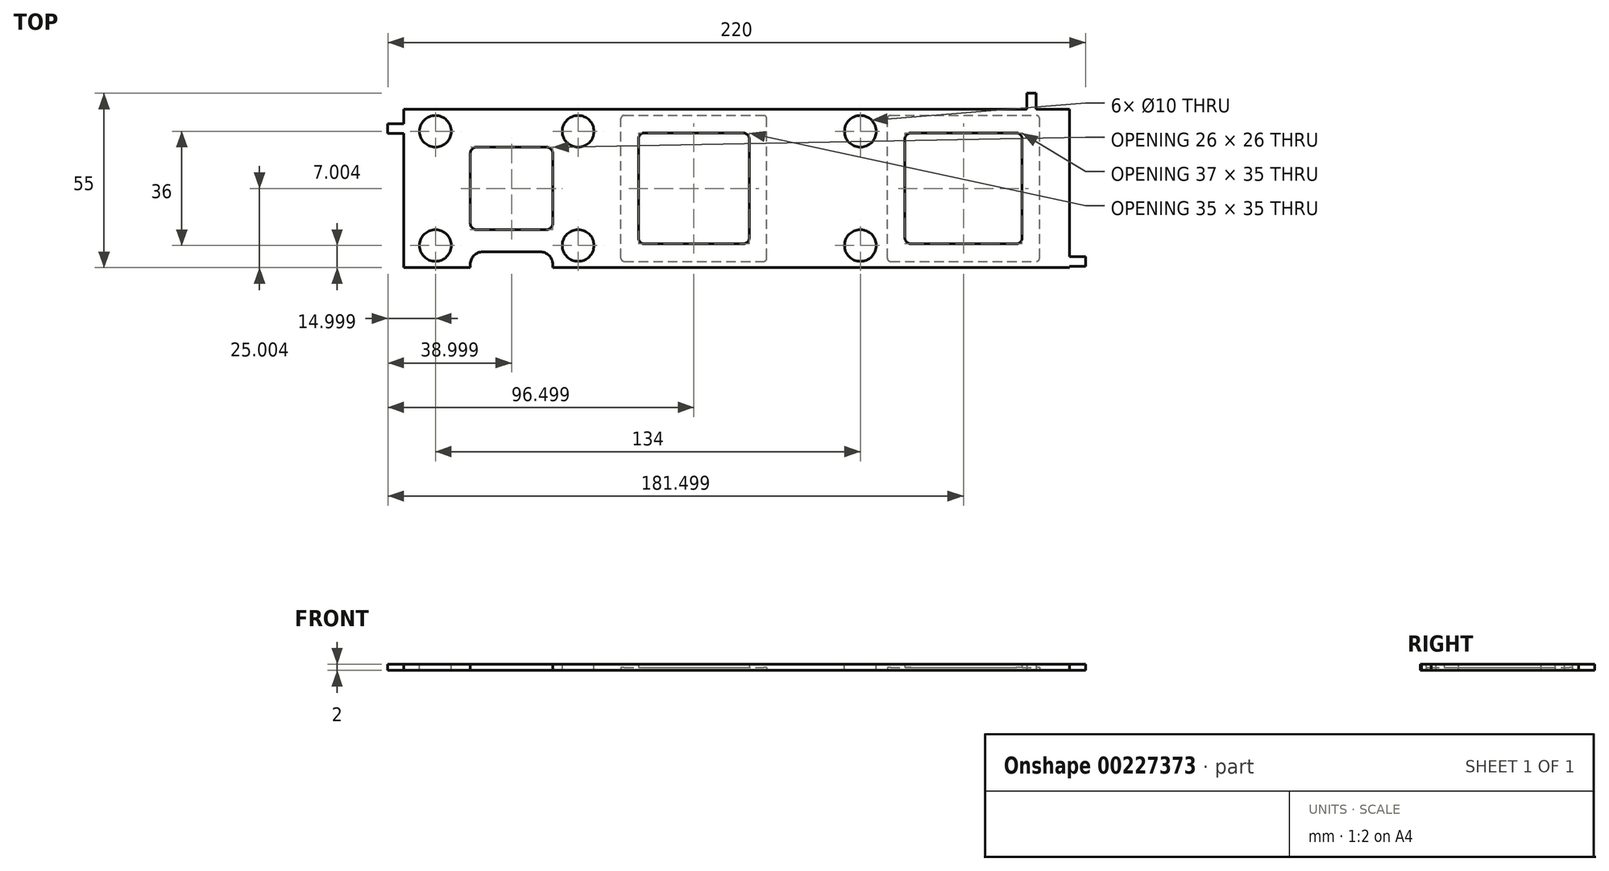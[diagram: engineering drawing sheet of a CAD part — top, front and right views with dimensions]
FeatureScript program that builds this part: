
annotation { "Feature Type Name" : "Feature", "Feature Type Description" : "" }
export const myFeature = defineFeature(function(context is Context, id is Id, definition is map)
    precondition{}
    {
        {
            var Q0;
            Q0=qCreatedBy(makeId("Top.planeOp"),FACE);
            var sketch = newSketch(context, id + "F0", { "sketchPlane" : qUnion([Q0])});
            skLineSegment(sketch, "E0.bottom", {"start": v(-23.9, 18.14) * mm, "end": v(186.1, 18.14) * mm});
            skLineSegment(sketch, "E0.top", {"start": v(-23.9, -31.86) * mm, "end": v(186.1, -31.86) * mm});
            skLineSegment(sketch, "E0.left", {"start": v(-23.9, 18.14) * mm, "end": v(-23.9, -31.86) * mm});
            skLineSegment(sketch, "E0.right", {"start": v(186.1, 18.14) * mm, "end": v(186.1, -31.86) * mm});
            skPoint(sketch, "E1.oppositeSnap0", {"position": v(-26.4, 18.14) * mm});
            skLineSegment(sketch, "E1.bottom", {"start": v(172.54, 23.14) * mm, "end": v(175.54, 23.14) * mm});
            skLineSegment(sketch, "E1.top", {"start": v(172.54, 18.14) * mm, "end": v(175.54, 18.14) * mm});
            skLineSegment(sketch, "E1.left", {"start": v(172.54, 23.14) * mm, "end": v(172.54, 18.14) * mm});
            skLineSegment(sketch, "E1.right", {"start": v(175.54, 23.14) * mm, "end": v(175.54, 18.14) * mm});
            skLineSegment(sketch, "E2.bottom", {"start": v(-9.51, -31.86) * mm, "end": v(-6.51, -31.86) * mm});
            skLineSegment(sketch, "E2.top", {"start": v(-9.51, -36.86) * mm, "end": v(-6.51, -36.86) * mm});
            skLineSegment(sketch, "E2.left", {"start": v(-9.51, -31.86) * mm, "end": v(-9.51, -36.86) * mm});
            skLineSegment(sketch, "E2.right", {"start": v(-6.51, -31.86) * mm, "end": v(-6.51, -36.86) * mm});
            skLineSegment(sketch, "E3.bottom", {"start": v(186.1, -28.4) * mm, "end": v(191.1, -28.4) * mm});
            skLineSegment(sketch, "E3.top", {"start": v(186.1, -31.4) * mm, "end": v(191.1, -31.4) * mm});
            skLineSegment(sketch, "E3.left", {"start": v(186.1, -28.4) * mm, "end": v(186.1, -31.4) * mm});
            skLineSegment(sketch, "E3.right", {"start": v(191.1, -28.4) * mm, "end": v(191.1, -31.4) * mm});
            skLineSegment(sketch, "E4.bottom", {"start": v(-28.9, 10.54) * mm, "end": v(-23.9, 10.54) * mm});
            skLineSegment(sketch, "E4.top", {"start": v(-28.9, 13.54) * mm, "end": v(-23.9, 13.54) * mm});
            skLineSegment(sketch, "E4.left", {"start": v(-28.9, 10.54) * mm, "end": v(-28.9, 13.54) * mm});
            skLineSegment(sketch, "E4.right", {"start": v(-23.9, 10.54) * mm, "end": v(-23.9, 13.54) * mm});
            skSolve(sketch);
        }
        {
            var Q0;
            Q0=makeQuery(id+"F0.imprint","IMPRINT",FACE,{"disambiguationData":[TD([[makeQuery(id+"F0.imprint","IMPRINT",EDGE,{"derivedFrom":sQuery(id+"F0.wireOp",EDGE,"E0.bottom")}),-1.0]])]});
            extrude(context, id + "F1", {"entities" : qUnion([Q0]), "depth" : 2 * mm});
        }
        {
            var Q0;
            Q0=makeQuery(id+"F1.opExtrude","CAP_FACE",FACE,{"disambiguationData":[OSD([sQuery(id+"F0.wireOp",EDGE,"E0.bottom"),sQuery(id+"F0.wireOp",EDGE,"E0.top"),sQuery(id+"F0.wireOp",EDGE,"E0.left"),sQuery(id+"F0.wireOp",EDGE,"E0.right")])],"isStart":true});
            var sketch = newSketch(context, id + "F2", { "sketchPlane" : qUnion([Q0])});
            skLineSegment(sketch, "E5.bottom", {"start": v(-2.9, 19.86) * mm, "end": v(23.1, 19.86) * mm});
            skLineSegment(sketch, "E5.top", {"start": v(-2.9, -6.14) * mm, "end": v(23.1, -6.14) * mm});
            skLineSegment(sketch, "E5.left", {"start": v(-2.9, 19.86) * mm, "end": v(-2.9, -6.14) * mm});
            skLineSegment(sketch, "E5.right", {"start": v(23.1, 19.86) * mm, "end": v(23.1, -6.14) * mm});
            skSolve(sketch);
        }
        {
            var Q0;
            Q0=makeQuery(id+"F2.imprint","IMPRINT",FACE,{"disambiguationData":[TD([[makeQuery(id+"F2.imprint","IMPRINT",EDGE,{"derivedFrom":sQuery(id+"F2.wireOp",EDGE,"E5.bottom")}),-1.0]])]});
            extrude(context, id + "F3", {"entities" : qUnion([Q0]), "operationType" : NewBodyOperationType.REMOVE, "oppositeDirection" : true, "depth" : 15.4 * mm});
        }
        {
            var Q0;
            Q0=makeQuery(id+"F1.opExtrude","CAP_FACE",FACE,{"disambiguationData":[OSD([sQuery(id+"F0.wireOp",EDGE,"E0.bottom"),sQuery(id+"F0.wireOp",EDGE,"E0.top"),sQuery(id+"F0.wireOp",EDGE,"E0.left"),sQuery(id+"F0.wireOp",EDGE,"E0.right")])],"isStart":true});
            var sketch = newSketch(context, id + "F4", { "sketchPlane" : qUnion([Q0])});
            skLineSegment(sketch, "E6.bottom", {"start": v(50.1, 24.36) * mm, "end": v(85.1, 24.36) * mm});
            skLineSegment(sketch, "E6.top", {"start": v(50.1, -10.64) * mm, "end": v(85.1, -10.64) * mm});
            skLineSegment(sketch, "E6.left", {"start": v(50.1, 24.36) * mm, "end": v(50.1, -10.64) * mm});
            skLineSegment(sketch, "E6.right", {"start": v(85.1, 24.36) * mm, "end": v(85.1, -10.64) * mm});
            skLineSegment(sketch, "E7.bottom", {"start": v(134.1, 24.36) * mm, "end": v(171.1, 24.36) * mm});
            skLineSegment(sketch, "E7.top", {"start": v(134.1, -10.64) * mm, "end": v(171.1, -10.64) * mm});
            skLineSegment(sketch, "E7.left", {"start": v(134.1, 24.36) * mm, "end": v(134.1, -10.64) * mm});
            skLineSegment(sketch, "E7.right", {"start": v(171.1, 24.36) * mm, "end": v(171.1, -10.64) * mm});
            skSolve(sketch);
        }
        {
            var Q0;
            Q0=makeQuery(id+"F4.imprint","IMPRINT",FACE,{"disambiguationData":[TD([[makeQuery(id+"F4.imprint","IMPRINT",EDGE,{"derivedFrom":sQuery(id+"F4.wireOp",EDGE,"E6.bottom")}),-1.0]])]});
            var Q1;
            Q1=makeQuery(id+"F4.imprint","IMPRINT",FACE,{"disambiguationData":[TD([[makeQuery(id+"F4.imprint","IMPRINT",EDGE,{"derivedFrom":sQuery(id+"F4.wireOp",EDGE,"E7.bottom")}),-1.0]])]});
            extrude(context, id + "F5", {"entities" : qUnion([Q0, Q1]), "operationType" : NewBodyOperationType.REMOVE, "oppositeDirection" : true, "depth" : 25 * mm});
        }
        {
            var Q0;
            Q0=makeQuery(id+"F1.opExtrude","CAP_FACE",FACE,{"disambiguationData":[OSD([sQuery(id+"F0.wireOp",EDGE,"E0.bottom"),sQuery(id+"F0.wireOp",EDGE,"E0.top"),sQuery(id+"F0.wireOp",EDGE,"E0.left"),sQuery(id+"F0.wireOp",EDGE,"E0.right")])],"isStart":false});
            var sketch = newSketch(context, id + "F6", { "sketchPlane" : qUnion([Q0])});
            skLineSegment(sketch, "E8.bottom", {"start": v(-2.9, -26.86) * mm, "end": v(23.1, -26.86) * mm});
            skLineSegment(sketch, "E8.top", {"start": v(-2.9, -31.86) * mm, "end": v(23.1, -31.86) * mm});
            skLineSegment(sketch, "E8.left", {"start": v(-2.9, -26.86) * mm, "end": v(-2.9, -31.86) * mm});
            skLineSegment(sketch, "E8.right", {"start": v(23.1, -26.86) * mm, "end": v(23.1, -31.86) * mm});
            skSolve(sketch);
        }
        {
            var Q0;
            Q0=makeQuery(id+"F6.imprint","IMPRINT",FACE,{"disambiguationData":[TD([[makeQuery(id+"F6.imprint","IMPRINT",EDGE,{"derivedFrom":sQuery(id+"F6.wireOp",EDGE,"E8.bottom")}),-1.0]])]});
            extrude(context, id + "F7", {"entities" : qUnion([Q0]), "operationType" : NewBodyOperationType.REMOVE, "oppositeDirection" : true, "depth" : 25 * mm});
        }
        {
            var Q0;
            Q0=makeQuery(id+"F7.boolean.opBoolean","COPY",EDGE,{"derivedFrom":makeQuery(id+"F7.opExtrude","SWEPT_EDGE",EDGE,{"disambiguationData":[OSD([sQuery(id+"F6.wireOp",EDGE,"E8.bottom"),sQuery(id+"F6.wireOp",EDGE,"E8.left")])]})});
            var Q1;
            Q1=makeQuery(id+"F7.boolean.opBoolean","COPY",EDGE,{"derivedFrom":makeQuery(id+"F7.opExtrude","SWEPT_EDGE",EDGE,{"disambiguationData":[OSD([sQuery(id+"F6.wireOp",EDGE,"E8.bottom"),sQuery(id+"F6.wireOp",EDGE,"E8.right")])]})});
            fillet(context, id + "F8", {"entities" : qUnion([Q0, Q1]), "radius" : 4 * mm, "tangentPropagation" : true, "allowEdgeOverflow" : false});
        }
        {
            var Q0;
            Q0=makeQuery(id+"F5.boolean.opBoolean","COPY",EDGE,{"derivedFrom":makeQuery(id+"F5.opExtrude","SWEPT_EDGE",EDGE,{"disambiguationData":[OSD([sQuery(id+"F4.wireOp",EDGE,"E6.top"),sQuery(id+"F4.wireOp",EDGE,"E6.left")])]})});
            var Q1;
            Q1=makeQuery(id+"F5.boolean.opBoolean","COPY",EDGE,{"derivedFrom":makeQuery(id+"F5.opExtrude","SWEPT_EDGE",EDGE,{"disambiguationData":[OSD([sQuery(id+"F4.wireOp",EDGE,"E6.top"),sQuery(id+"F4.wireOp",EDGE,"E6.right")])]})});
            var Q2;
            Q2=makeQuery(id+"F5.boolean.opBoolean","COPY",EDGE,{"derivedFrom":makeQuery(id+"F5.opExtrude","SWEPT_EDGE",EDGE,{"disambiguationData":[OSD([sQuery(id+"F4.wireOp",EDGE,"E6.bottom"),sQuery(id+"F4.wireOp",EDGE,"E6.left")])]})});
            var Q3;
            Q3=makeQuery(id+"F5.boolean.opBoolean","COPY",EDGE,{"derivedFrom":makeQuery(id+"F5.opExtrude","SWEPT_EDGE",EDGE,{"disambiguationData":[OSD([sQuery(id+"F4.wireOp",EDGE,"E7.bottom"),sQuery(id+"F4.wireOp",EDGE,"E7.left")])]})});
            var Q4;
            Q4=makeQuery(id+"F5.boolean.opBoolean","COPY",EDGE,{"derivedFrom":makeQuery(id+"F5.opExtrude","SWEPT_EDGE",EDGE,{"disambiguationData":[OSD([sQuery(id+"F4.wireOp",EDGE,"E6.bottom"),sQuery(id+"F4.wireOp",EDGE,"E6.right")])]})});
            var Q5;
            Q5=makeQuery(id+"F5.boolean.opBoolean","COPY",EDGE,{"derivedFrom":makeQuery(id+"F5.opExtrude","SWEPT_EDGE",EDGE,{"disambiguationData":[OSD([sQuery(id+"F4.wireOp",EDGE,"E7.bottom"),sQuery(id+"F4.wireOp",EDGE,"E7.right")])]})});
            var Q6;
            Q6=makeQuery(id+"F5.boolean.opBoolean","COPY",EDGE,{"derivedFrom":makeQuery(id+"F5.opExtrude","SWEPT_EDGE",EDGE,{"disambiguationData":[OSD([sQuery(id+"F4.wireOp",EDGE,"E7.top"),sQuery(id+"F4.wireOp",EDGE,"E7.left")])]})});
            var Q7;
            Q7=makeQuery(id+"F5.boolean.opBoolean","COPY",EDGE,{"derivedFrom":makeQuery(id+"F5.opExtrude","SWEPT_EDGE",EDGE,{"disambiguationData":[OSD([sQuery(id+"F4.wireOp",EDGE,"E7.top"),sQuery(id+"F4.wireOp",EDGE,"E7.right")])]})});
            var Q8;
            Q8=makeQuery(id+"F3.boolean.opBoolean","COPY",EDGE,{"derivedFrom":makeQuery(id+"F3.opExtrude","SWEPT_EDGE",EDGE,{"disambiguationData":[OSD([sQuery(id+"F2.wireOp",EDGE,"E5.top"),sQuery(id+"F2.wireOp",EDGE,"E5.right")])]})});
            var Q9;
            Q9=makeQuery(id+"F3.boolean.opBoolean","COPY",EDGE,{"derivedFrom":makeQuery(id+"F3.opExtrude","SWEPT_EDGE",EDGE,{"disambiguationData":[OSD([sQuery(id+"F2.wireOp",EDGE,"E5.top"),sQuery(id+"F2.wireOp",EDGE,"E5.left")])]})});
            var Q10;
            Q10=makeQuery(id+"F3.boolean.opBoolean","COPY",EDGE,{"derivedFrom":makeQuery(id+"F3.opExtrude","SWEPT_EDGE",EDGE,{"disambiguationData":[OSD([sQuery(id+"F2.wireOp",EDGE,"E5.bottom"),sQuery(id+"F2.wireOp",EDGE,"E5.right")])]})});
            var Q11;
            Q11=makeQuery(id+"F3.boolean.opBoolean","COPY",EDGE,{"derivedFrom":makeQuery(id+"F3.opExtrude","SWEPT_EDGE",EDGE,{"disambiguationData":[OSD([sQuery(id+"F2.wireOp",EDGE,"E5.bottom"),sQuery(id+"F2.wireOp",EDGE,"E5.left")])]})});
            fillet(context, id + "F9", {"entities" : qUnion([Q0, Q1, Q2, Q3, Q4, Q5, Q6, Q7, Q8, Q9, Q10, Q11]), "radius" : 2 * mm, "tangentPropagation" : true, "allowEdgeOverflow" : false});
        }
        {
            var Q0;
            Q0=makeQuery(id+"F1.opExtrude","CAP_FACE",FACE,{"disambiguationData":[OSD([sQuery(id+"F0.wireOp",EDGE,"E0.bottom"),sQuery(id+"F0.wireOp",EDGE,"E0.top"),sQuery(id+"F0.wireOp",EDGE,"E0.left"),sQuery(id+"F0.wireOp",EDGE,"E0.right")])],"isStart":false});
            var sketch = newSketch(context, id + "F10", { "sketchPlane" : qUnion([Q0])});
            skCircle(sketch, "E9", {"center": v(-13.9, 11.14) * mm, "radius": 5 * mm});
            skCircle(sketch, "E10", {"center": v(-13.9, -24.86) * mm, "radius": 5 * mm});
            skCircle(sketch, "E11", {"center": v(31.1, -24.86) * mm, "radius": 5 * mm});
            skCircle(sketch, "E12", {"center": v(120.1, 11.14) * mm, "radius": 5 * mm});
            skCircle(sketch, "E13", {"center": v(120.1, -24.86) * mm, "radius": 5 * mm});
            skSolve(sketch);
        }
        {
            var Q0;
            Q0=makeQuery(id+"F10.imprint","IMPRINT",FACE,{"disambiguationData":[TD([[makeQuery(id+"F10.imprint","IMPRINT",EDGE,{"derivedFrom":sQuery(id+"F10.wireOp",EDGE,"E12")}),1.0]])]});
            var Q1;
            Q1=makeQuery(id+"F10.imprint","IMPRINT",FACE,{"disambiguationData":[TD([[makeQuery(id+"F10.imprint","IMPRINT",EDGE,{"derivedFrom":sQuery(id+"F10.wireOp",EDGE,"E13")}),1.0]])]});
            var Q2;
            Q2=makeQuery(id+"F10.imprint","IMPRINT",FACE,{"disambiguationData":[TD([[makeQuery(id+"F10.imprint","IMPRINT",EDGE,{"derivedFrom":sQuery(id+"F10.wireOp",EDGE,"E11")}),1.0]])]});
            var Q3;
            Q3=makeQuery(id+"F10.imprint","IMPRINT",FACE,{"disambiguationData":[TD([[makeQuery(id+"F10.imprint","IMPRINT",EDGE,{"derivedFrom":sQuery(id+"F10.wireOp",EDGE,"izE0OuF1-xiSJ-FB18-c39p-0N1t3OY4qnCi")}),1.0]])]});
            var Q4;
            Q4=makeQuery(id+"F10.imprint","IMPRINT",FACE,{"disambiguationData":[TD([[makeQuery(id+"F10.imprint","IMPRINT",EDGE,{"derivedFrom":sQuery(id+"F10.wireOp",EDGE,"E9")}),1.0]])]});
            var Q5;
            Q5=makeQuery(id+"F10.imprint","IMPRINT",FACE,{"disambiguationData":[TD([[makeQuery(id+"F10.imprint","IMPRINT",EDGE,{"derivedFrom":sQuery(id+"F10.wireOp",EDGE,"E10")}),1.0]])]});
            var Q6;
            Q6=sQuery(id+"F10.wireOp",EDGE,"E9");
            var Q7;
            Q7=sQuery(id+"F10.wireOp",EDGE,"E10");
            var Q8;
            Q8=sQuery(id+"F10.wireOp",EDGE,"E11");
            var Q9;
            Q9=sQuery(id+"F10.wireOp",EDGE,"izE0OuF1-xiSJ-FB18-c39p-0N1t3OY4qnCi");
            var Q10;
            Q10=sQuery(id+"F10.wireOp",EDGE,"E12");
            var Q11;
            Q11=sQuery(id+"F10.wireOp",EDGE,"E13");
            extrude(context, id + "F11", {"entities" : qUnion([Q0, Q1, Q2, Q3, Q4, Q5]), "operationType" : NewBodyOperationType.REMOVE, "surfaceEntities" : qUnion([Q6, Q7, Q8, Q9, Q10, Q11]), "oppositeDirection" : true, "depth" : 25 * mm});
        }
        {
            var Q0;
            Q0=makeQuery(id+"F1.opExtrude","CAP_FACE",FACE,{"disambiguationData":[OSD([sQuery(id+"F0.wireOp",EDGE,"E0.bottom"),sQuery(id+"F0.wireOp",EDGE,"E0.top"),sQuery(id+"F0.wireOp",EDGE,"E0.left"),sQuery(id+"F0.wireOp",EDGE,"E0.right")])],"isStart":false});
            var sketch = newSketch(context, id + "F12", { "sketchPlane" : qUnion([Q0])});
            skCircle(sketch, "E14", {"center": v(31.1, 11.14) * mm, "radius": 5 * mm});
            skSolve(sketch);
        }
        {
            var Q0;
            Q0=qSketchRegion(id+"F12",true);
            extrude(context, id + "F13", {"entities" : qUnion([Q0]), "operationType" : NewBodyOperationType.REMOVE, "oppositeDirection" : true, "depth" : 25 * mm});
        }
        {
            var Q0;
            Q0=makeQuery(id+"F0.imprint","IMPRINT",FACE,{"disambiguationData":[TD([[makeQuery(id+"F0.imprint","IMPRINT",EDGE,{"derivedFrom":sQuery(id+"F0.wireOp",EDGE,"E0.bottom")}),-1.0]])]});
            var sketch = newSketch(context, id + "F14", { "sketchPlane" : qUnion([Q0])});
            skLineSegment(sketch, "E15.bottom", {"start": v(44.6, -29.86) * mm, "end": v(90.6, -29.86) * mm});
            skLineSegment(sketch, "E15.top", {"start": v(44.6, 16.14) * mm, "end": v(90.6, 16.14) * mm});
            skLineSegment(sketch, "E15.left", {"start": v(44.6, -29.86) * mm, "end": v(44.6, 16.14) * mm});
            skLineSegment(sketch, "E15.right", {"start": v(90.6, -29.86) * mm, "end": v(90.6, 16.14) * mm});
            skLineSegment(sketch, "E16.bottom", {"start": v(128.6, -29.86) * mm, "end": v(176.6, -29.86) * mm});
            skLineSegment(sketch, "E16.top", {"start": v(128.6, 16.14) * mm, "end": v(176.6, 16.14) * mm});
            skLineSegment(sketch, "E16.left", {"start": v(128.6, -29.86) * mm, "end": v(128.6, 16.14) * mm});
            skLineSegment(sketch, "E16.right", {"start": v(176.6, -29.86) * mm, "end": v(176.6, 16.14) * mm});
            skSolve(sketch);
        }
        {
            var Q0;
            Q0=qSketchRegion(id+"F14",true);
            extrude(context, id + "F15", {"entities" : qUnion([Q0]), "operationType" : NewBodyOperationType.REMOVE, "depth" : 1 * mm});
        }
        {
            var Q0;
            Q0=makeQuery(id+"F15.boolean.opBoolean","COPY",EDGE,{"derivedFrom":makeQuery(id+"F15.opExtrude","SWEPT_EDGE",EDGE,{"disambiguationData":[OSD([sQuery(id+"F14.wireOp",EDGE,"E15.bottom"),sQuery(id+"F14.wireOp",EDGE,"E15.left")])]})});
            var Q1;
            Q1=makeQuery(id+"F15.boolean.opBoolean","COPY",EDGE,{"derivedFrom":makeQuery(id+"F15.opExtrude","SWEPT_EDGE",EDGE,{"disambiguationData":[OSD([sQuery(id+"F14.wireOp",EDGE,"E15.bottom"),sQuery(id+"F14.wireOp",EDGE,"E15.right")])]})});
            var Q2;
            Q2=makeQuery(id+"F15.boolean.opBoolean","COPY",EDGE,{"derivedFrom":makeQuery(id+"F15.opExtrude","SWEPT_EDGE",EDGE,{"disambiguationData":[OSD([sQuery(id+"F14.wireOp",EDGE,"E15.top"),sQuery(id+"F14.wireOp",EDGE,"E15.right")])]})});
            var Q3;
            Q3=makeQuery(id+"F15.boolean.opBoolean","COPY",EDGE,{"derivedFrom":makeQuery(id+"F15.opExtrude","SWEPT_EDGE",EDGE,{"disambiguationData":[OSD([sQuery(id+"F14.wireOp",EDGE,"E15.top"),sQuery(id+"F14.wireOp",EDGE,"E15.left")])]})});
            fillet(context, id + "F16", {"entities" : qUnion([Q0, Q1, Q2, Q3]), "radius" : 1 * mm, "tangentPropagation" : true, "allowEdgeOverflow" : false});
        }
        {
            var Q0;
            Q0=makeQuery(id+"F15.boolean.opBoolean","COPY",EDGE,{"derivedFrom":makeQuery(id+"F15.opExtrude","SWEPT_EDGE",EDGE,{"disambiguationData":[OSD([sQuery(id+"F14.wireOp",EDGE,"E16.bottom"),sQuery(id+"F14.wireOp",EDGE,"E16.left")])]})});
            var Q1;
            Q1=makeQuery(id+"F15.boolean.opBoolean","COPY",EDGE,{"derivedFrom":makeQuery(id+"F15.opExtrude","SWEPT_EDGE",EDGE,{"disambiguationData":[OSD([sQuery(id+"F14.wireOp",EDGE,"E16.bottom"),sQuery(id+"F14.wireOp",EDGE,"E16.right")])]})});
            var Q2;
            Q2=makeQuery(id+"F15.boolean.opBoolean","COPY",EDGE,{"derivedFrom":makeQuery(id+"F15.opExtrude","SWEPT_EDGE",EDGE,{"disambiguationData":[OSD([sQuery(id+"F14.wireOp",EDGE,"E16.top"),sQuery(id+"F14.wireOp",EDGE,"E16.right")])]})});
            var Q3;
            Q3=makeQuery(id+"F15.boolean.opBoolean","COPY",EDGE,{"derivedFrom":makeQuery(id+"F15.opExtrude","SWEPT_EDGE",EDGE,{"disambiguationData":[OSD([sQuery(id+"F14.wireOp",EDGE,"E16.top"),sQuery(id+"F14.wireOp",EDGE,"E16.left")])]})});
            fillet(context, id + "F17", {"entities" : qUnion([Q0, Q1, Q2, Q3]), "radius" : 1 * mm, "tangentPropagation" : true, "allowEdgeOverflow" : false});
        }
        {
            var Q0;
            Q0=makeQuery(id+"F0.imprint","IMPRINT",FACE,{"disambiguationData":[TD([[makeQuery(id+"F0.imprint","IMPRINT",EDGE,{"derivedFrom":sQuery(id+"F0.wireOp",EDGE,"E3.bottom")}),-1.0]])]});
            var Q1;
            Q1=makeQuery(id+"F0.imprint","IMPRINT",FACE,{"disambiguationData":[TD([[makeQuery(id+"F0.imprint","IMPRINT",EDGE,{"derivedFrom":sQuery(id+"F0.wireOp",EDGE,"E1.bottom")}),-1.0]])]});
            var Q2;
            Q2=makeQuery(id+"F0.imprint","IMPRINT",FACE,{"disambiguationData":[TD([[makeQuery(id+"F0.imprint","IMPRINT",EDGE,{"derivedFrom":sQuery(id+"F0.wireOp",EDGE,"gMm37RoQ-QMnn-3wSX-GLZN-vOBIeoNuV8F2.bottom")}),-1.0]])]});
            var Q3;
            Q3=makeQuery(id+"F0.imprint","IMPRINT",FACE,{"disambiguationData":[TD([[makeQuery(id+"F0.imprint","IMPRINT",EDGE,{"derivedFrom":sQuery(id+"F0.wireOp",EDGE,"E2.bottom")}),-1.0]])]});
            var Q4;
            Q4=makeQuery(id+"F0.imprint","IMPRINT",FACE,{"disambiguationData":[TD([[makeQuery(id+"F0.imprint","IMPRINT",EDGE,{"derivedFrom":sQuery(id+"F0.wireOp",EDGE,"E4.bottom")}),1.0]])]});
            extrude(context, id + "F18", {"entities" : qUnion([Q0, Q1, Q2, Q3, Q4]), "operationType" : NewBodyOperationType.ADD, "depth" : 2 * mm});
        }
    });
